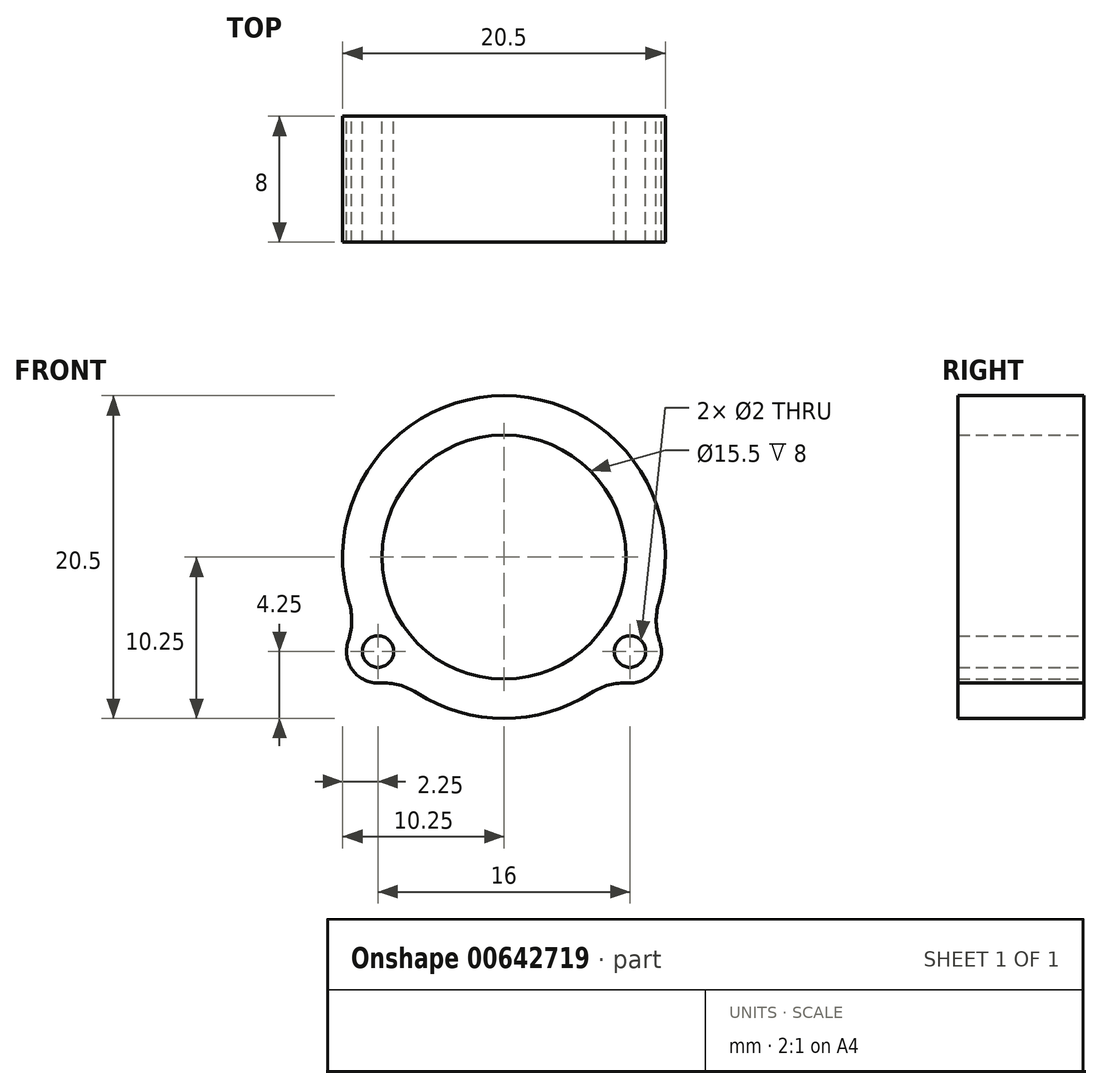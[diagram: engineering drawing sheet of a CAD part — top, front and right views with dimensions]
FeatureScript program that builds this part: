
annotation { "Feature Type Name" : "Feature", "Feature Type Description" : "" }
export const myFeature = defineFeature(function(context is Context, id is Id, definition is map)
    precondition{}
    {
        {
            var Q0;
            Q0=qCreatedBy(makeId("Front.planeOp"),FACE);
            var sketch = newSketch(context, id + "F0", { "sketchPlane" : qUnion([Q0])});
            skCircle(sketch, "E0", {"center": v(0, 0) * mm, "radius": 7.75 * mm});
            skArc(sketch, "E1", {"start": v(7.9, -8) * mm, "mid": v(9.6, -7.2) * mm, "end": v(9.89, -5.34) * mm});
            skArc(sketch, "E2", {"start": v(-9.89, -5.34) * mm, "mid": v(-9.6, -7.2) * mm, "end": v(-7.9, -8) * mm});
            skPoint(sketch, "E3.orphan", {"position": v(7, -6) * mm});
            skPoint(sketch, "E4.orphan", {"position": v(-11.68, -0.75) * mm});
            skPoint(sketch, "E5.start.orphan", {"position": v(-4.9, -6) * mm});
            skArc(sketch, "E6.trimOffspring", {"start": v(-5.54, -8.63) * mm, "mid": v(0, -10.25) * mm, "end": v(5.54, -8.63) * mm});
            skArc(sketch, "E7.trimOffspring", {"start": v(9.83, -2.9) * mm, "mid": v(0, 10.25) * mm, "end": v(-9.83, -2.9) * mm});
            skCircle(sketch, "E8", {"center": v(-8, -6) * mm, "radius": 1 * mm});
            skCircle(sketch, "E9", {"center": v(8, -6) * mm, "radius": 1 * mm});
            skPoint(sketch, "E10.visualSharp", {"position": v(9.24, -4.43) * mm});
            skArc(sketch, "E10.filletArc", {"start": v(9.83, -2.9) * mm, "mid": v(9.67, -4.13) * mm, "end": v(9.89, -5.34) * mm});
            skPoint(sketch, "E11.visualSharp", {"position": v(6.84, -7.63) * mm});
            skArc(sketch, "E11.filletArc", {"start": v(7.9, -8) * mm, "mid": v(6.67, -8.13) * mm, "end": v(5.54, -8.63) * mm});
            skPoint(sketch, "E12.visualSharp", {"position": v(-9.24, -4.43) * mm});
            skArc(sketch, "E12.filletArc", {"start": v(-9.89, -5.34) * mm, "mid": v(-9.67, -4.13) * mm, "end": v(-9.83, -2.9) * mm});
            skPoint(sketch, "E13.visualSharp", {"position": v(-6.84, -7.63) * mm});
            skArc(sketch, "E13.filletArc", {"start": v(-5.54, -8.63) * mm, "mid": v(-6.67, -8.13) * mm, "end": v(-7.9, -8) * mm});
            skSolve(sketch);
        }
        {
            var Q0;
            Q0=makeQuery(id+"F0.imprint","IMPRINT",FACE,{"disambiguationData":[TD([[makeQuery(id+"F0.imprint","IMPRINT",EDGE,{"derivedFrom":sQuery(id+"F0.wireOp",EDGE,"E0")}),-1.0]])]});
            extrude(context, id + "F1", {"entities" : qUnion([Q0]), "depth" : 8 * mm, "offsetDistance" : 25 * mm});
        }
    });
